# Revit family: Systemlösung Überspannungsableiter V20 im Gehäuse 1-polig_3-polig + NPE
name_source: partatom
category: Generic Models
revit_build: Autodesk Revit 2015 (Build: 20140606_1530(x64)
units: mm (PartAtom-declared; Revit-internal decimal feet)

## types (2) — shared parameters
Diameter = 36 mm
Diameter 1 = 30 mm  [stored 0.0984252 ft]
Height = 94 mm  [stored 0.308399 ft]
Height 1 = 63 mm
Length = 190 mm
Manufacturer = OBO Bettermann
Material = OBO PP
Material 2 = PC
Material 3 = OBO TPE
URL = http://www.obo-bettermann.com
Width = 150 mm

## per-type parameters (varying)
| type | GTIN | Manufacturer Art.No. |
| VG-V20-1+NPE-280 | 4012196423194 | 5095381 |
| VG-V20-3+NPE-280 | 4012196423200 | 5095383 |

note: column(s) folded — value = type name in every type: Article Type

note: [stored X ft] marks values corroborated as IEEE doubles in the binary element streams (Revit-internal decimal feet)

## geometry (parser evidence)
native form markers: Sweep x2
no freeform markers — native parametric forms only
